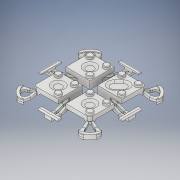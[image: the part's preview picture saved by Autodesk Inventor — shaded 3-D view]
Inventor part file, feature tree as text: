
AUTODESK INVENTOR PART (.ipt)
format: ipt  version: 2018 (Build 220112000, 112)  size: 3,035,136 bytes
history: native  units: in
note: dims shown in document units (in); Inventor stores cm internally (conversion verified against a paired STEP export)
features: other x29, extrude x17, sketch x10, loft x6, fillet x5, thicken_offset x3, chamfer x3, pattern_circular x3, projected_geometry x3, mirror x2, plane x2
ambient origin geometry x8: Origin, YZ Plane, XZ Plane, XY Plane, X Axis, Y Axis, Z Axis, Center Point
bodies: Solid40 (feature_tree), Solid47 (feature_tree), Solid48 (feature_tree), Solid52 (feature_tree)
feature tree (83):
  other  "Remote Shell.ipt"
  other  "Remote Top.ipt"
  other  "Split plane"
  other  "Top of Top Plane"
  other  "Button Base Sketch"
  other  "Peg Sketch"
  extrude  "Extrusion18"  Depth=0.3937in
  other  "Button Bottom Plane"
  other  "Button Mirror Plane1"
  other  "Button Mirror Plane2"
  sketch  "Sketch89"  dims[d420=1.5748in d421=360.0deg d441=0.3937in]
  extrude  "Extrusion28"  Depth=0.06in
  extrude  "Extrusion30"  Depth=0.025in
  extrude  "Extrusion29"  Depth=1.5748in TaperAngle=360.0deg
  extrude  "Extrusion33"  [1 undecoded]
  extrude  "Extrusion32"  Depth=0.0625in
  extrude  "Extrusion34"  Depth=0.25in
  thicken_offset  "Thicken7"
  loft  "Loft23"
  loft  "Loft22"
  extrude  "Extrusion48"  Depth=0.075in
  fillet  "Fillet30"  Radius=0.075in
  fillet  "Fillet31"  Radius=0.05in
  mirror  "Mirror13"
  other  "Model Bottom Plane"
  other  "Paddle Sketch"
  extrude  "Extrusion38"  Depth=0.0125in
  extrude  "Extrusion47"  Depth=0.02in
  extrude  "Extrusion41"  Depth=0.0125in
  thicken_offset  "Thicken4"
  thicken_offset  "Thicken5"
  loft  "Loft20"
  loft  "Loft21"
  extrude  "Extrusion42"  Depth=0.06in
  extrude  "Extrusion44"  Depth=1.5748in TaperAngle=360.0deg
  chamfer  "Chamfer1"  Distance=0.0125in
  chamfer  "Chamfer4"  Distance=0.02in
  fillet  "Fillet32"  Radius=0.0125in
  fillet  "Fillet34"  Radius=0.02in
  other  "Button Actuator Boss"
  fillet  "Fillet5"  Radius=0.15in
  pattern_circular  "Circular Pattern4"  [2 undecoded]
  plane  "Work Plane48"
  extrude  "Extrusion10"  Depth=0.07in
  extrude  "Extrusion14"  Depth=0.02in
  pattern_circular  "Circular Pattern3"  [2 undecoded]
  extrude  "Extrusion15"  Depth=0.075in
  loft  "Loft16"
  pattern_circular  "Circular Pattern6"  [2 undecoded]
  sketch  "Sketch83"  dims[d382=0.025in d383=-0.4466in d389=-0.015in]
  sketch  "Sketch84"  dims[d403=45.0deg d404=0.0625in]
  plane  "Work Plane54"
  loft  "Loft17"
  mirror  "Mirror15"
  extrude  "Extrusion45"  Depth=0.075in
  chamfer  "Chamfer5"  Distance=0.075in
  other  "TaggingFeature2"
  sketch  "Sketch22"  dims[d13=0.3937in d0=0.3937in]
  other  "TaggingFeature4"
  other  "Srf5"
  projected_geometry  "Projected Loop6"
  sketch  "Sketch80"  dims[d221=0.02in d222=0.0in d353=0.025in]
  sketch  "Sketch82"  dims[d374=0.025in d375=-0.4466in d377=1.5748in d378=360.0deg]
  sketch  "Sketch85"  dims[d405=45.0deg d406=0.25in]
  other  "Button Peg Sketch"
  projected_geometry  "Projected Loop7"
  other  "Button Paddle Sketch"
  other  "Pattern of Solid48:9"
  sketch  "Sketch94"  dims[d442=0.075in d443=0.075in]
  other  "Edges15"
  projected_geometry  "Projected Loop9"
  other  "Edges14"
  other  "Edges20"
  other  "Edges24"
  other  "Edges21"
  other  "Edges25"
  sketch  "Sketch97"  dims[d444=0.075in d445=0.075in d446=0.075in d447=0.05in d448=0.0in d488=0.0125in d489=0.02in d490=0.0125in d491=0.02in d492=0.02in d493=0.06in d494=0.0in d495=90.0deg d496=0.0in d497=90.0deg d498=0.0in d499=90.0deg d500=1.5748in d501=360.0deg d503=0.0125in d504=0.02in d505=0.0125in d506=0.02in d507=0.15in d508=0.885in d509=0.07in d510=0.02in d511=0.0in d512=90.0deg d513=0.0in d514=90.0deg d515=0.0in d516=90.0deg d517=0.02in d525=0.075in d526=0.075in d527=0.075in d528=0.075in d529=0.075in d530=0.075in d531=0.075in d540=0.05in d542=0.07in d543=0.0in d544=0.09in d545=0.0in d546=0.03in d547=0.0in d551=0.015in d552=0.015in d553=0.055in d554=0.0in d555=0.07in d556=0.0in d557=0.025in d558=0.0in d565=0.25in d570=90.0deg d574=0.07in d575=0.125in d576=45.0deg d593=0.001in d594=0.0in d595=0.001in d596=0.0in d597=0.005in d598=0.0in d603=0.06in d604=0.06in d605=0.03in d606=0.03in d613=0.05in d614=0.0in d631=0.025in d633=0.075in d652=0.05in d653=0.0in d654=0.124in d655=0.0in d658=0.01in d659=0.01in d660=0.0in d661=90.0deg d662=0.0in d663=90.0deg d664=0.05in d665=0.05in d666=0.0in d667=90.0deg d668=0.0in d669=90.0deg d670=0.03in d671=0.0in d672=90.0deg d673=0.02in d674=0.5497in d675=0.02in d676=0.0687in d678=0.05in d679=0.275in d680=0.275in d681=0.5497in d682=0.0687in d683=0.05in d684=0.05in d685=0.05in d694=0.025in d695=0.1in d696=0.025in d697=0.1in d698=90.0deg d699=0.05in d700=0.125in d701=30.0deg d702=0.1in d703=0.05in d704=0.05in d705=0.05in d706=0.05in d707=0.031in d708=0.0in d709=0.01in d710=0.01in d711=0.04in d712=0.04in d713=0.015in d714=0.015in d715=0.0in d716=90.0deg d719=0.02in d720=0.02in d721=0.02in d722=0.02in d723=0.1249in d724=1.5748in d726=360.0deg d728=0.15in d729=0.7874in d731=0.625in d732=0.7874in d734=0.625in d737=0.075in d738=-0.0206in d741=0.09in d742=0.0in d745=0.0in d746=90.0deg d749=0.12in d750=0.1in d751=0.12in d752=0.1in d753=0.0in d754=90.0deg d755=0.0in d756=90.0deg d757=0.05in d758=0.05in d759=0.07in d761=0.05in d762=0.01in d763=0.125in d764=45.0deg d767=0.005in d768=0.005in d769=0.0001in d770=0.0001in d771=0.0001in d772=0.7874in d774=0.625in d775=0.7874in d777=0.625in d780=1.0in d781=0.0in]
  other  "Solid1::Remote Top.ipt"
  other  "Srf2"
  sketch  "Sketch44"  dims[d108=0.0in d109=0.09in d110=0.09in d111=0.12in d112=0.38in d113=0.0137in d114=0.0069in d115=1.5748in d117=0.015in d118=0.02in d119=0.06in d120=0.03in d121=0.0687in d122=0.0172in d123=0.0in d124=0.0in d125=0.0in d126=360.0deg d217=0.06in d218=0.06in d219=0.03in d220=0.03in]
  other  "Srf1::Derived"
  other  "Top Solid::Remote Shell.ipt"
  other  "Srf6"
note: 7 required parameter values undecoded (feature->parameter linkage not recoverable at this tier; creation-order binding heuristic only, values carry confidence <= 0.55)
